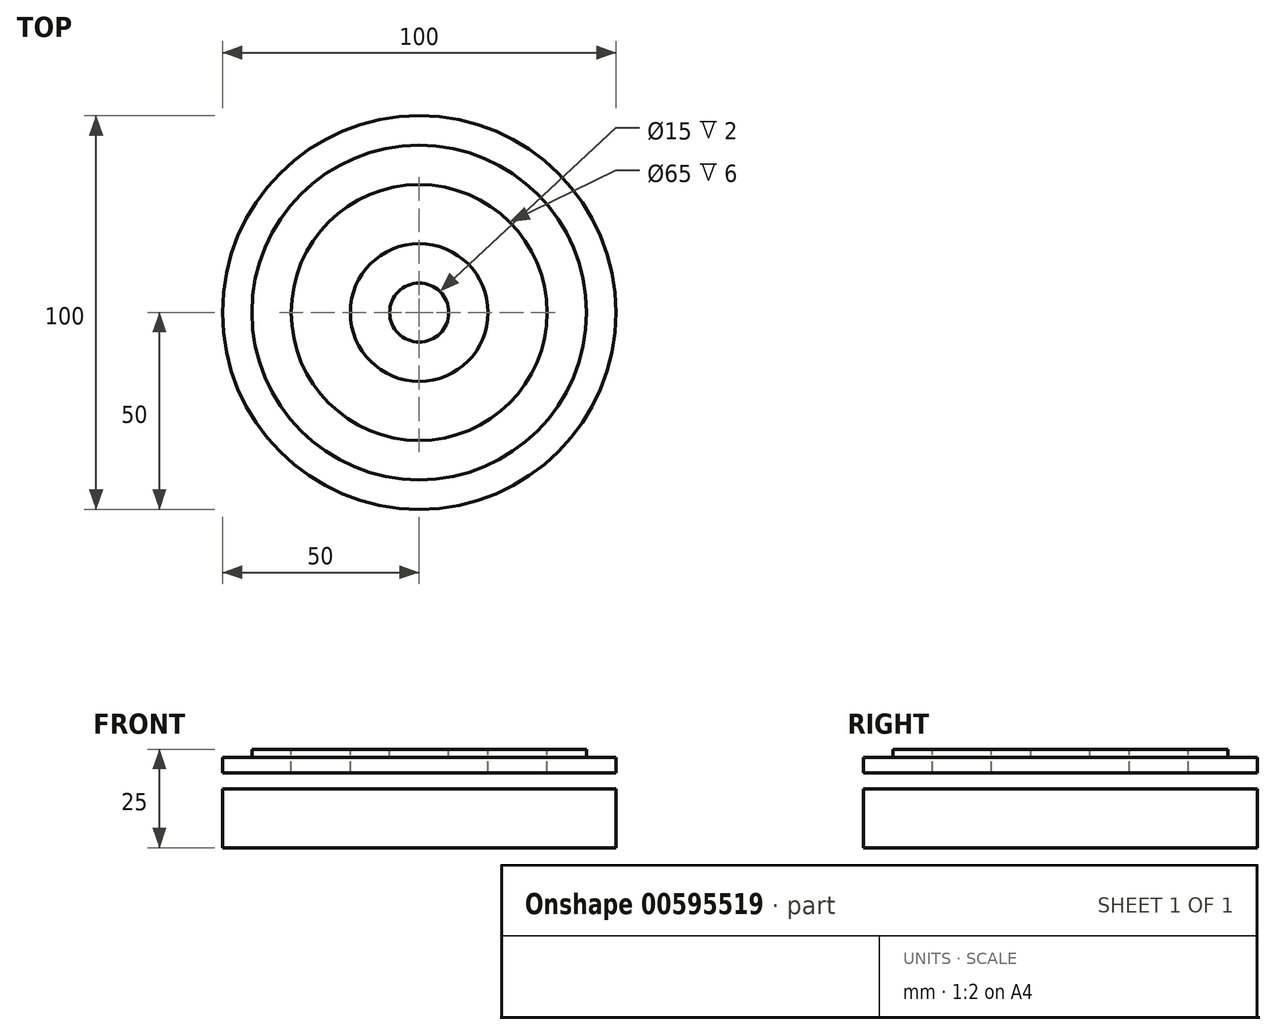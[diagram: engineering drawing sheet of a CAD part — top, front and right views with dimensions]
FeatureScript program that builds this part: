
annotation { "Feature Type Name" : "Feature", "Feature Type Description" : "" }
export const myFeature = defineFeature(function(context is Context, id is Id, definition is map)
    precondition{}
    {
        {
            var Q0;
            Q0=qCreatedBy(makeId("Front.planeOp"),FACE);
            var sketch = newSketch(context, id + "F0", { "sketchPlane" : qUnion([Q0])});
            skLineSegment(sketch, "E0.bottom", {"start": v(0, 0) * mm, "end": v(50, 0) * mm});
            skLineSegment(sketch, "E0.top", {"start": v(0, 15) * mm, "end": v(50, 15) * mm});
            skLineSegment(sketch, "E0.left", {"start": v(0, 0) * mm, "end": v(0, 15) * mm});
            skLineSegment(sketch, "E0.right", {"start": v(50, 0) * mm, "end": v(50, 15) * mm});
            skLineSegment(sketch, "E1.bottom", {"start": v(17.5, 15) * mm, "end": v(32.5, 15) * mm});
            skLineSegment(sketch, "E1.top", {"start": v(17.5, 25) * mm, "end": v(32.5, 25) * mm});
            skLineSegment(sketch, "E1.left", {"start": v(17.5, 15) * mm, "end": v(17.5, 25) * mm});
            skLineSegment(sketch, "E1.right", {"start": v(32.5, 15) * mm, "end": v(32.5, 25) * mm});
            skLineSegment(sketch, "E2.bottom", {"start": v(17.5, 25) * mm, "end": v(7.5, 25) * mm});
            skLineSegment(sketch, "E2.top", {"start": v(17.5, 23) * mm, "end": v(7.5, 23) * mm});
            skLineSegment(sketch, "E2.left", {"start": v(17.5, 25) * mm, "end": v(17.5, 23) * mm});
            skLineSegment(sketch, "E2.right", {"start": v(7.5, 25) * mm, "end": v(7.5, 23) * mm});
            skLineSegment(sketch, "E3.bottom", {"start": v(32.5, 25) * mm, "end": v(42.5, 25) * mm});
            skLineSegment(sketch, "E3.top", {"start": v(32.5, 23) * mm, "end": v(42.5, 23) * mm});
            skLineSegment(sketch, "E3.left", {"start": v(32.5, 25) * mm, "end": v(32.5, 23) * mm});
            skLineSegment(sketch, "E3.right", {"start": v(42.5, 25) * mm, "end": v(42.5, 23) * mm});
            skLineSegment(sketch, "E4", {"start": v(42.5, 23) * mm, "end": v(50, 23) * mm});
            skLineSegment(sketch, "E5", {"start": v(7.5, 23) * mm, "end": v(0, 23) * mm});
            skLineSegment(sketch, "E6", {"start": v(0, 23) * mm, "end": v(0, 19) * mm});
            skLineSegment(sketch, "E7", {"start": v(50, 23) * mm, "end": v(50, 19) * mm});
            skLineSegment(sketch, "E8", {"start": v(0, 19) * mm, "end": v(17.5, 19) * mm});
            skLineSegment(sketch, "E9", {"start": v(50, 19) * mm, "end": v(32.5, 19) * mm});
            skSolve(sketch);
        }
        {
            var Q0;
            Q0=makeQuery(id+"F0.imprint","IMPRINT",FACE,{"disambiguationData":[TD([[makeQuery(id+"F0.imprint","IMPRINT",EDGE,{"derivedFrom":sQuery(id+"F0.wireOp",EDGE,"E0.bottom")}),1.0]])]});
            var Q1;
            {var subQ3=sQuery(id+"F0.wireOp",EDGE,"E1.bottom");Q1=makeQuery(id+"F0.imprint","IMPRINT",FACE,{"disambiguationData":[TD([[makeQuery(id+"F0.imprint","IMPRINT",EDGE,{"derivedFrom":subQ3}),1.0]])]});}
            var Q2;
            {var subQ0=sQuery(id+"F0.wireOp",EDGE,"E2.top");Q2=makeQuery(id+"F0.imprint","IMPRINT",FACE,{"disambiguationData":[TD([[makeQuery(id+"F0.imprint","IMPRINT",EDGE,{"derivedFrom":subQ0}),1.0]])]});}
            var Q3;
            Q3=makeQuery(id+"F0.imprint","IMPRINT",FACE,{"disambiguationData":[TD([[makeQuery(id+"F0.imprint","IMPRINT",EDGE,{"derivedFrom":sQuery(id+"F0.wireOp",EDGE,"E2.bottom")}),1.0]])]});
            var Q4;
            Q4=makeQuery(id+"F0.imprint","IMPRINT",FACE,{"disambiguationData":[TD([[makeQuery(id+"F0.imprint","IMPRINT",EDGE,{"derivedFrom":sQuery(id+"F0.wireOp",EDGE,"E3.bottom")}),-1.0]])]});
            var Q5;
            {var subQ0=sQuery(id+"F0.wireOp",EDGE,"E3.top");Q5=makeQuery(id+"F0.imprint","IMPRINT",FACE,{"disambiguationData":[TD([[makeQuery(id+"F0.imprint","IMPRINT",EDGE,{"derivedFrom":subQ0}),-1.0]])]});}
            var Q6;
            Q6=sQuery(id+"F0.wireOp",EDGE,"E6");
            revolve(context, id + "F1", {"entities" : qUnion([Q0, Q1, Q2, Q3, Q4, Q5]), "axis" : qUnion([Q6]), "revolveType" : RevolveType.FULL});
        }
    });
